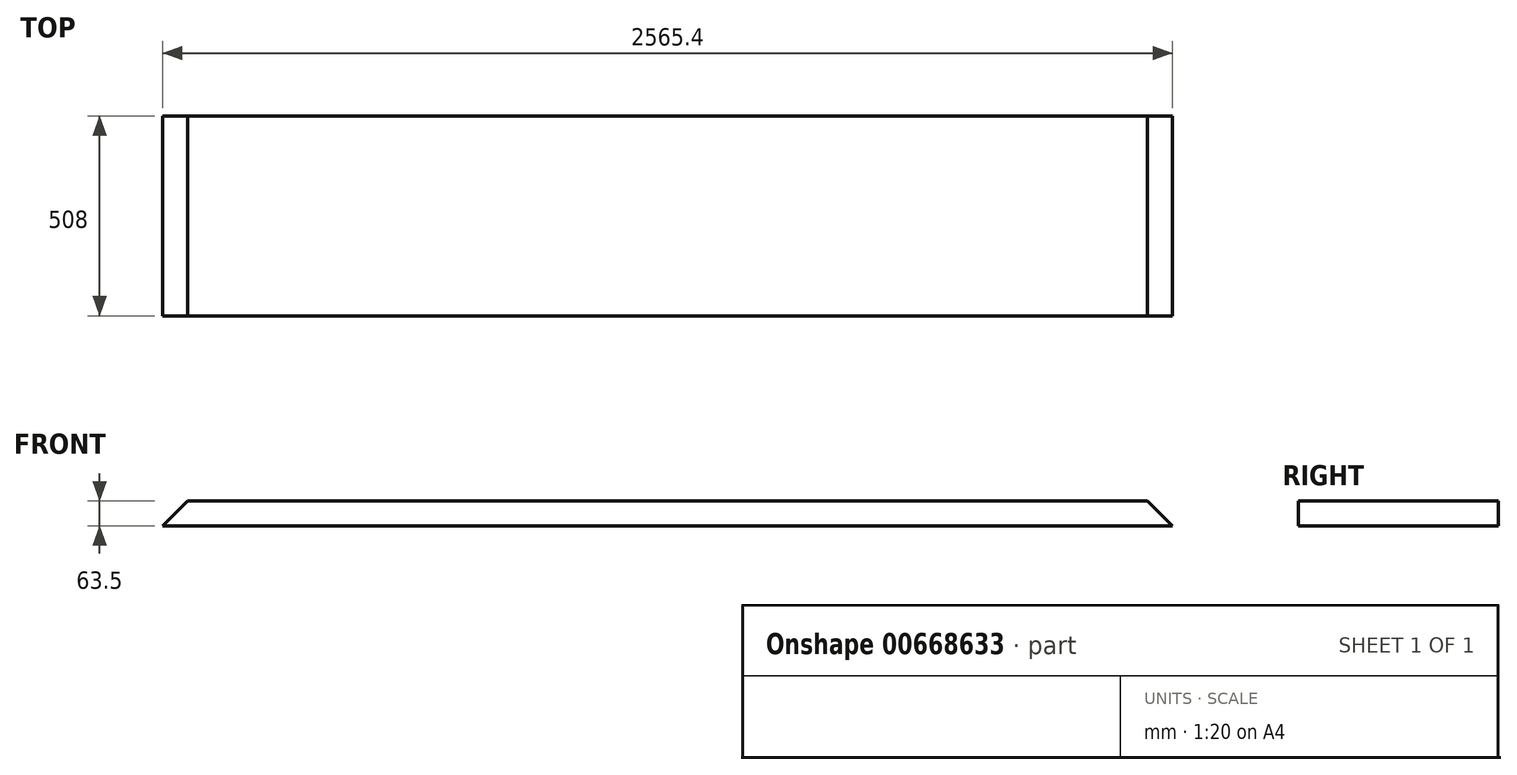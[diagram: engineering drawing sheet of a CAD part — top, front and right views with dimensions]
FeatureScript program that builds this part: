
annotation { "Feature Type Name" : "Feature", "Feature Type Description" : "" }
export const myFeature = defineFeature(function(context is Context, id is Id, definition is map)
    precondition{}
    {
        {
            var Q0;
            Q0=qCreatedBy(makeId("Top.planeOp"),FACE);
            var sketch = newSketch(context, id + "F0", { "sketchPlane" : qUnion([Q0])});
            skLineSegment(sketch, "E0.bottom", {"start": v(-1282.7, 254) * mm, "end": v(1282.7, 254) * mm});
            skLineSegment(sketch, "E0.top", {"start": v(-1282.7, -254) * mm, "end": v(1282.7, -254) * mm});
            skLineSegment(sketch, "E0.left", {"start": v(-1282.7, 254) * mm, "end": v(-1282.7, -254) * mm});
            skLineSegment(sketch, "E0.right", {"start": v(1282.7, 254) * mm, "end": v(1282.7, -254) * mm});
            skSolve(sketch);
        }
        {
            var Q0;
            Q0=makeQuery(id+"F0.imprint","IMPRINT",FACE,{"disambiguationData":[TD([[makeQuery(id+"F0.imprint","IMPRINT",EDGE,{"derivedFrom":sQuery(id+"F0.wireOp",EDGE,"E0.bottom")}),-1.0]])]});
            extrude(context, id + "F1", {"entities" : qUnion([Q0]), "depth" : 63.5 * mm, "offsetDistance" : 25.4 * mm, "symmetric" : true});
        }
        {
            var Q0;
            Q0=makeQuery(id+"F1.opExtrude","SWEPT_FACE",FACE,{"disambiguationData":[OSD([sQuery(id+"F0.wireOp",EDGE,"E0.bottom")])]});
            var sketch = newSketch(context, id + "F2", { "sketchPlane" : qUnion([Q0])});
            skLineSegment(sketch, "E1", {"start": v(1282.7, -31.75) * mm, "end": v(1282.7, 31.75) * mm});
            skLineSegment(sketch, "E2", {"start": v(1282.7, 31.75) * mm, "end": v(1219.2, 31.75) * mm});
            skLineSegment(sketch, "E3", {"start": v(1219.2, 31.75) * mm, "end": v(1282.7, -31.75) * mm});
            skLineSegment(sketch, "E4", {"start": v(-1282.7, -31.75) * mm, "end": v(-1282.7, 31.75) * mm});
            skLineSegment(sketch, "E5", {"start": v(-1282.7, 31.75) * mm, "end": v(-1219.2, 31.75) * mm});
            skLineSegment(sketch, "E6", {"start": v(-1219.2, 31.75) * mm, "end": v(-1282.7, -31.75) * mm});
            skSolve(sketch);
        }
        {
            var Q0;
            Q0 = qSketchRegion(id + "F2", true);
            extrude(context, id + "F3", {"entities" : qUnion([Q0]), "operationType" : NewBodyOperationType.REMOVE, "endBound" : BoundingType.THROUGH_ALL, "oppositeDirection" : true, "depth" : 25.4 * mm, "offsetDistance" : 25.4 * mm});
        }
    });
